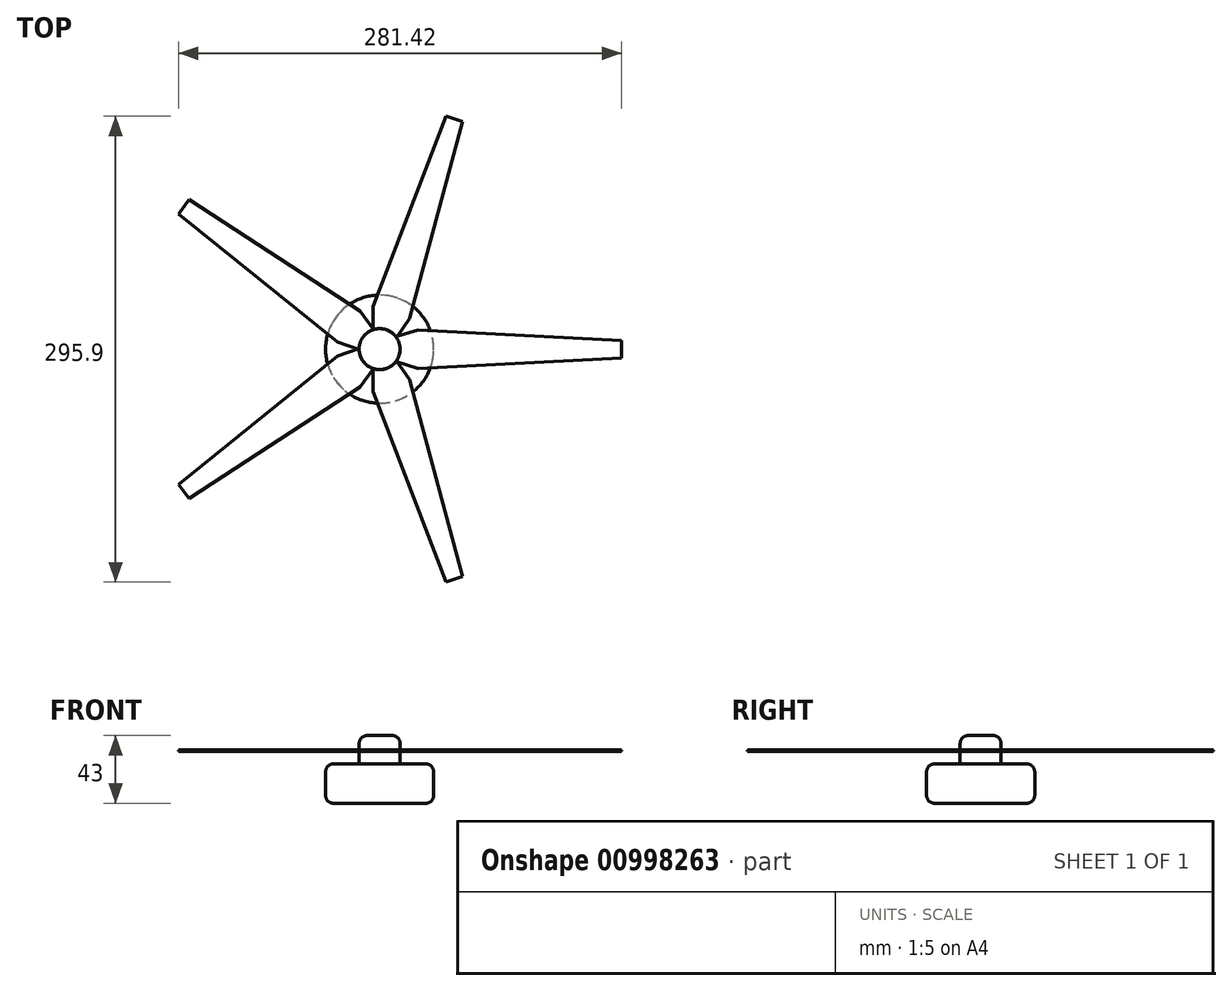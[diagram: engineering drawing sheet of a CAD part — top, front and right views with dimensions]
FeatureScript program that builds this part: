
annotation { "Feature Type Name" : "Feature", "Feature Type Description" : "" }
export const myFeature = defineFeature(function(context is Context, id is Id, definition is map)
    precondition{}
    {
        {
            var Q0;
            Q0=qCreatedBy(makeId("Top.planeOp"),FACE);
            var sketch = newSketch(context, id + "F0", { "sketchPlane" : qUnion([Q0])});
            skCircle(sketch, "E0", {"center": v(0, 0) * mm, "radius": 34.35 * mm});
            skSolve(sketch);
        }
        {
            var Q0;
            Q0=makeQuery(id+"F0.imprint","IMPRINT",FACE,{"disambiguationData":[TD([[makeQuery(id+"F0.imprint","IMPRINT",EDGE,{"derivedFrom":sQuery(id+"F0.wireOp",EDGE,"E0")}),1.0]])]});
            extrude(context, id + "F1", {"entities" : qUnion([Q0]), "depth" : 25 * mm, "offsetDistance" : 25 * mm});
        }
        {
            var Q0;
            Q0=makeQuery(id+"F1.opExtrude","CAP_FACE",FACE,{"disambiguationData":[OSD([sQuery(id+"F0.wireOp",EDGE,"E0")])],"isStart":false});
            var sketch = newSketch(context, id + "F2", { "sketchPlane" : qUnion([Q0])});
            skCircle(sketch, "E1", {"center": v(0, 0) * mm, "radius": 13 * mm});
            skSolve(sketch);
        }
        {
            var Q0;
            Q0=makeQuery(id+"F2.imprint","IMPRINT",FACE,{"disambiguationData":[TD([[makeQuery(id+"F2.imprint","IMPRINT",EDGE,{"derivedFrom":sQuery(id+"F2.wireOp",EDGE,"E1")}),1.0]])]});
            extrude(context, id + "F3", {"entities" : qUnion([Q0]), "operationType" : NewBodyOperationType.ADD, "depth" : 18 * mm, "offsetDistance" : 25 * mm});
        }
        {
            var Q0;
            Q0=makeQuery(id+"F3.opExtrude","CAP_EDGE",EDGE,{"disambiguationData":[OSD([sQuery(id+"F2.wireOp",EDGE,"E1")])],"isStart":false});
            var Q1;
            Q1=makeQuery(id+"F1.opExtrude","CAP_EDGE",EDGE,{"disambiguationData":[OSD([sQuery(id+"F0.wireOp",EDGE,"E0")])],"isStart":false});
            var Q2;
            Q2=makeQuery(id+"F1.opExtrude","CAP_EDGE",EDGE,{"disambiguationData":[OSD([sQuery(id+"F0.wireOp",EDGE,"E0")])],"isStart":true});
            fillet(context, id + "F4", {"entities" : qUnion([Q0, Q1, Q2]), "radius" : 5 * mm, "tangentPropagation" : true, "allowEdgeOverflow" : false});
        }
        {
            var Q0;
            Q0=makeQuery(id+"F3.opExtrude","CAP_FACE",FACE,{"disambiguationData":[OSD([sQuery(id+"F2.wireOp",EDGE,"E1")])],"isStart":false});
            cPlane(context, id + "F5", {"entities" : qUnion([Q0]), "cplaneType" : CPlaneType.OFFSET, "offset" : 10 * mm, "oppositeDirection" : true, "width" : 150 * mm, "height" : 150 * mm});
        }
        {
            var Q0;
            Q0=qCreatedBy(id+"F5.planeOp",FACE);
            var sketch = newSketch(context, id + "F6", { "sketchPlane" : qUnion([Q0])});
            skLineSegment(sketch, "E2", {"start": v(0, 0) * mm, "end": v(4.74, 6.15) * mm});
            skLineSegment(sketch, "E3", {"start": v(4.74, 6.15) * mm, "end": v(24.38, 12.17) * mm});
            skLineSegment(sketch, "E4", {"start": v(24.38, 12.17) * mm, "end": v(153.76, 5.56) * mm});
            skLineSegment(sketch, "E5", {"start": v(153.76, 5.56) * mm, "end": v(153.76, 0) * mm});
            skLineSegment(sketch, "E6.MirrorCS", {"start": v(24.38, -12.17) * mm, "end": v(153.76, -5.56) * mm});
            skLineSegment(sketch, "E7.MirrorCS", {"start": v(0, 0) * mm, "end": v(4.74, -6.15) * mm});
            skLineSegment(sketch, "E8.MirrorCS", {"start": v(4.74, -6.15) * mm, "end": v(24.38, -12.17) * mm});
            skLineSegment(sketch, "E9", {"start": v(153.76, 0) * mm, "end": v(153.76, -5.56) * mm});
            skSolve(sketch);
        }
        {
            var Q0;
            Q0=makeQuery(id+"F6.imprint","IMPRINT",FACE,{"disambiguationData":[TD([[makeQuery(id+"F6.imprint","IMPRINT",EDGE,{"derivedFrom":sQuery(id+"F6.wireOp",EDGE,"E2")}),-1.0]])]});
            extrude(context, id + "F7", {"entities" : qUnion([Q0]), "operationType" : NewBodyOperationType.ADD, "depth" : 1 * mm, "offsetDistance" : 25 * mm});
        }
        {
            var Q0;
            Q0=makeQuery(id+"F1.opExtrude","SWEPT_BODY",BODY,{"disambiguationData":[OSD([sQuery(id+"F0.wireOp",EDGE,"E0")])]});
            var Q1;
            {var subQ0=sQuery(id+"F2.wireOp",EDGE,"E1");Q1=makeQuery(id+"F4.opFillet","BLEND_EDGE",EDGE,{"blendedFrom":[makeQuery(id+"F3.opExtrude","CAP_EDGE",EDGE,{"disambiguationData":[OSD([subQ0])],"isStart":false}),makeQuery(id+"F3.opExtrude","CAP_FACE",FACE,{"disambiguationData":[OSD([subQ0])],"isStart":false})],"blendedInto":[makeQuery(id+"F3.opExtrude","CAP_FACE",FACE,{"disambiguationData":[OSD([subQ0])],"isStart":false})]});}
            circularPattern(context, id + "F8", {"entities" : qUnion([Q0]), "axis" : qUnion([Q1]), "angle" : 360 * degree, "instanceCount" : 5, "equalSpace" : true});
        }
    });
